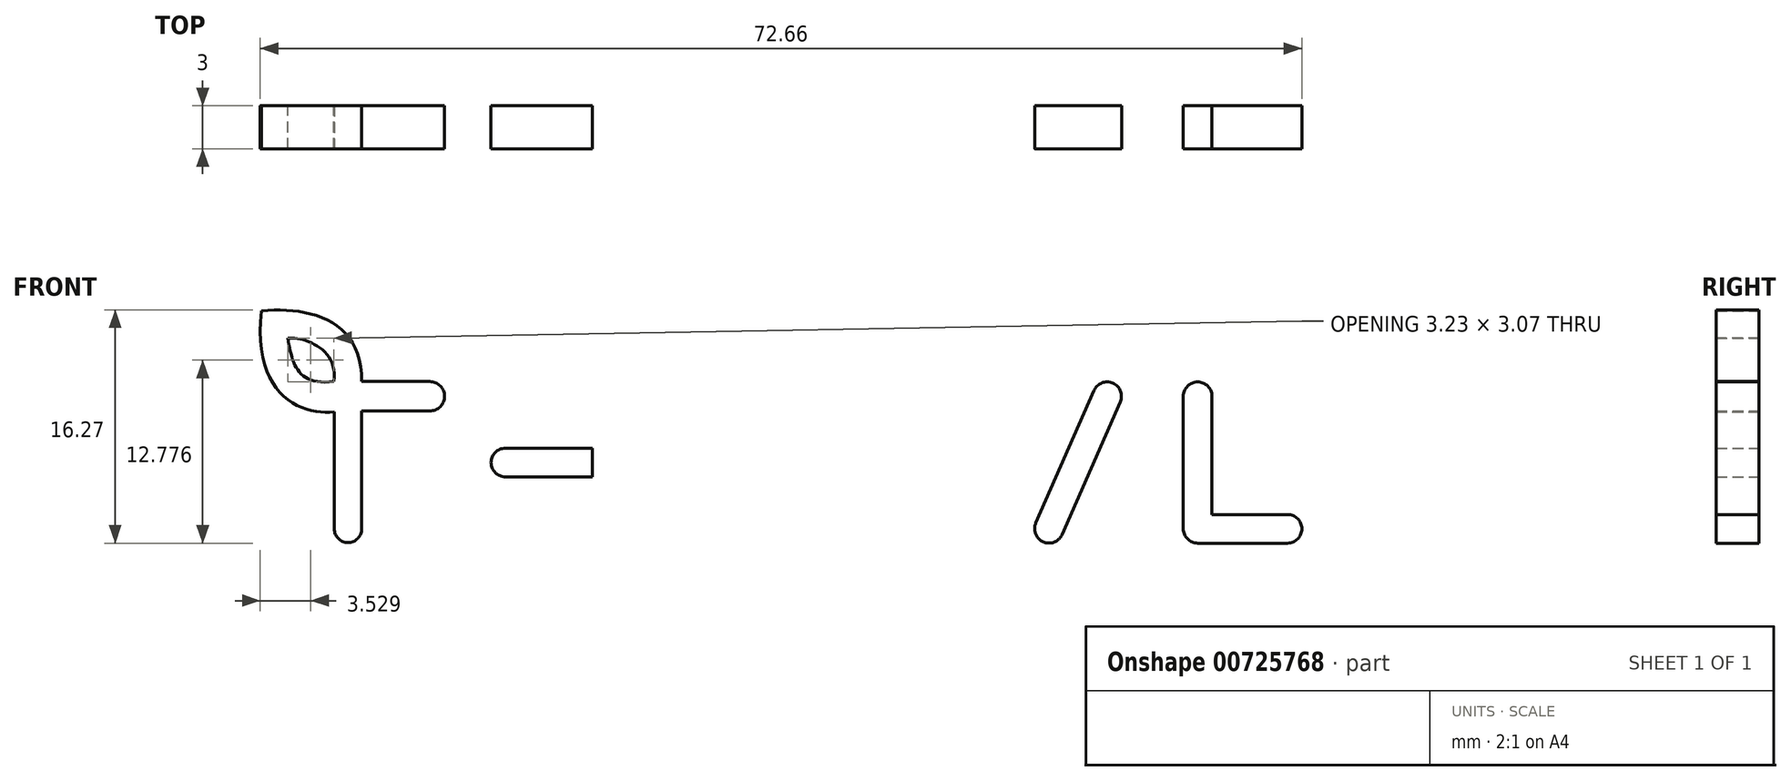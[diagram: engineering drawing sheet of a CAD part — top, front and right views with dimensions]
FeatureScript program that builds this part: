
annotation { "Feature Type Name" : "Feature", "Feature Type Description" : "" }
export const myFeature = defineFeature(function(context is Context, id is Id, definition is map)
    precondition{}
    {
        {
            var Q0;
            Q0=qCreatedBy(makeId("Front.planeOp"),FACE);
            var sketch = newSketch(context, id + "F0", { "sketchPlane" : qUnion([Q0])});
            skLineSegment(sketch, "E0.bottom", {"start": v(0, 0) * mm, "end": v(75, 0) * mm, "construction": true});
            skLineSegment(sketch, "E0.top", {"start": v(0, 50) * mm, "end": v(75, 50) * mm, "construction": true});
            skLineSegment(sketch, "E0.left", {"start": v(0, 0) * mm, "end": v(0, 50) * mm, "construction": true});
            skLineSegment(sketch, "E0.right", {"start": v(75, 0) * mm, "end": v(75, 50) * mm, "construction": true});
            skLineSegment(sketch, "E1", {"start": v(7.84, 1.22) * mm, "end": v(7.84, 9.44) * mm});
            skLineSegment(sketch, "E2", {"start": v(5.93, 1.22) * mm, "end": v(5.93, 9.38) * mm});
            skLineSegment(sketch, "E3", {"start": v(12.6, 9.44) * mm, "end": v(7.84, 9.44) * mm});
            skLineSegment(sketch, "E4", {"start": v(12.6, 11.5) * mm, "end": v(7.84, 11.5) * mm});
            skFitSpline(sketch, "E5", {"points": [v(7.84, 11.5) * mm, v(0.86, 16.42) * mm], "startDerivative": vector(0.22, 12.8) * mm, "endDerivative": vector(-9.91, -1.11) * mm});
            skFitSpline(sketch, "E6", {"points": [v(5.9, 11.5) * mm, v(2.68, 14.53) * mm], "startDerivative": vector(1.06, 6.93) * mm, "endDerivative": vector(-3.29, -0.35) * mm});
            skFitSpline(sketch, "E7", {"points": [v(5.93, 9.38) * mm, v(0.86, 16.42) * mm], "startDerivative": vector(-6.88, -0.84) * mm, "endDerivative": vector(2.12, 17.54) * mm});
            skFitSpline(sketch, "E8", {"points": [v(5.9, 11.5) * mm, v(2.68, 14.53) * mm], "startDerivative": vector(-7.74, -0.96) * mm, "endDerivative": vector(-0.91, 5.16) * mm});
            skArc(sketch, "E9", {"start": v(12.6, 11.5) * mm, "mid": v(13.62, 10.47) * mm, "end": v(12.6, 9.44) * mm});
            skArc(sketch, "E10", {"start": v(5.93, 1.22) * mm, "mid": v(6.89, 0.26) * mm, "end": v(7.84, 1.22) * mm});
            skLineSegment(sketch, "E11", {"start": v(17.86, 10.47) * mm, "end": v(17.86, 1.22) * mm, "construction": true});
            skPoint(sketch, "E11.startSnap0", {"position": v(13.62, 10.47) * mm});
            skLineSegment(sketch, "E12", {"start": v(24.94, 10.47) * mm, "end": v(24.94, 1.22) * mm, "construction": true});
            skLineSegment(sketch, "E13", {"start": v(17.86, 5.85) * mm, "end": v(24.94, 5.85) * mm, "construction": true});
            skArc(sketch, "E14.0.startCap", {"start": v(16.86, 10.47) * mm, "mid": v(17.86, 11.47) * mm, "end": v(18.86, 10.47) * mm});
            skArc(sketch, "E14.0.endCap", {"start": v(18.86, 1.22) * mm, "mid": v(17.86, 0.22) * mm, "end": v(16.86, 1.22) * mm});
            skLineSegment(sketch, "E14.0.left", {"start": v(18.86, 10.47) * mm, "end": v(18.86, 1.22) * mm});
            skLineSegment(sketch, "E14.0.right", {"start": v(16.86, 10.47) * mm, "end": v(16.86, 1.22) * mm});
            skArc(sketch, "E15.0.startCap", {"start": v(17.86, 4.85) * mm, "mid": v(16.86, 5.85) * mm, "end": v(17.86, 6.85) * mm});
            skArc(sketch, "E15.0.endCap", {"start": v(24.94, 6.85) * mm, "mid": v(25.94, 5.85) * mm, "end": v(24.94, 4.85) * mm});
            skLineSegment(sketch, "E15.0.left", {"start": v(17.86, 6.85) * mm, "end": v(24.94, 6.85) * mm});
            skLineSegment(sketch, "E15.0.right", {"start": v(17.86, 4.85) * mm, "end": v(24.94, 4.85) * mm});
            skArc(sketch, "E15.1.startCap", {"start": v(23.94, 10.47) * mm, "mid": v(24.94, 11.47) * mm, "end": v(25.94, 10.47) * mm});
            skArc(sketch, "E15.1.endCap", {"start": v(25.94, 1.22) * mm, "mid": v(24.94, 0.22) * mm, "end": v(23.94, 1.22) * mm});
            skLineSegment(sketch, "E15.1.left", {"start": v(25.94, 10.47) * mm, "end": v(25.94, 1.22) * mm});
            skLineSegment(sketch, "E15.1.right", {"start": v(23.94, 10.47) * mm, "end": v(23.94, 1.22) * mm});
            skLineSegment(sketch, "E16", {"start": v(31.54, 1.22) * mm, "end": v(31.54, 10.47) * mm, "construction": true});
            skLineSegment(sketch, "E17", {"start": v(31.54, 10.47) * mm, "end": v(35.35, 10.47) * mm, "construction": true});
            skLineSegment(sketch, "E18", {"start": v(31.54, 5) * mm, "end": v(35.5, 5) * mm, "construction": true});
            skLineSegment(sketch, "E19", {"start": v(35.5, 5) * mm, "end": v(38.46, 1.22) * mm, "construction": true});
            skFitSpline(sketch, "E20", {"points": [v(35.35, 10.47) * mm, v(35.5, 5) * mm], "startDerivative": vector(12.83, -0.22) * mm, "endDerivative": vector(-12.36, -0.46) * mm, "construction": true});
            skLineSegment(sketch, "E21", {"start": v(45.46, 1.22) * mm, "end": v(45.46, 10.47) * mm, "construction": true});
            skLineSegment(sketch, "E22", {"start": v(51.6, 10.47) * mm, "end": v(55.78, 1.22) * mm, "construction": true});
            skLineSegment(sketch, "E23", {"start": v(55.78, 1.22) * mm, "end": v(59.84, 10.47) * mm, "construction": true});
            skArc(sketch, "E24.0.startCap", {"start": v(50.69, 10.06) * mm, "mid": v(51.18, 11.38) * mm, "end": v(52.5, 10.88) * mm});
            skArc(sketch, "E24.0.endCap", {"start": v(56.7, 1.63) * mm, "mid": v(56.2, 0.31) * mm, "end": v(54.87, 0.8) * mm});
            skLineSegment(sketch, "E24.0.left", {"start": v(52.5, 10.88) * mm, "end": v(56.7, 1.63) * mm});
            skLineSegment(sketch, "E24.0.right", {"start": v(50.69, 10.06) * mm, "end": v(54.87, 0.8) * mm});
            skArc(sketch, "E24.1.startCap", {"start": v(56.7, 0.82) * mm, "mid": v(55.38, 0.3) * mm, "end": v(54.87, 1.62) * mm});
            skArc(sketch, "E24.1.endCap", {"start": v(58.92, 10.87) * mm, "mid": v(60.24, 11.38) * mm, "end": v(60.76, 10.07) * mm});
            skLineSegment(sketch, "E24.1.left", {"start": v(54.87, 1.62) * mm, "end": v(58.92, 10.87) * mm});
            skLineSegment(sketch, "E24.1.right", {"start": v(56.7, 0.82) * mm, "end": v(60.76, 10.07) * mm});
            skArc(sketch, "E25.0.startCap", {"start": v(46.46, 1.22) * mm, "mid": v(45.46, 0.22) * mm, "end": v(44.46, 1.22) * mm});
            skArc(sketch, "E25.0.endCap", {"start": v(44.46, 10.47) * mm, "mid": v(45.46, 11.47) * mm, "end": v(46.46, 10.47) * mm});
            skLineSegment(sketch, "E25.0.left", {"start": v(44.46, 1.22) * mm, "end": v(44.46, 10.47) * mm});
            skLineSegment(sketch, "E25.0.right", {"start": v(46.46, 1.22) * mm, "end": v(46.46, 10.47) * mm});
            skLineSegment(sketch, "E26", {"start": v(66.15, 10.47) * mm, "end": v(72.42, 10.47) * mm, "construction": true});
            skLineSegment(sketch, "E27", {"start": v(66.15, 1.22) * mm, "end": v(72.42, 1.22) * mm, "construction": true});
            skLineSegment(sketch, "E28", {"start": v(66.15, 5.85) * mm, "end": v(71.55, 5.85) * mm, "construction": true});
            skArc(sketch, "E29.0.startCap", {"start": v(66.15, 9.47) * mm, "mid": v(65.15, 10.47) * mm, "end": v(66.15, 11.47) * mm});
            skArc(sketch, "E29.0.endCap", {"start": v(72.42, 11.47) * mm, "mid": v(73.42, 10.47) * mm, "end": v(72.42, 9.47) * mm});
            skLineSegment(sketch, "E29.0.left", {"start": v(66.15, 11.47) * mm, "end": v(72.42, 11.47) * mm});
            skLineSegment(sketch, "E29.0.right", {"start": v(66.15, 9.47) * mm, "end": v(72.42, 9.47) * mm});
            skArc(sketch, "E29.1.startCap", {"start": v(67.15, 1.22) * mm, "mid": v(66.15, 0.22) * mm, "end": v(65.15, 1.22) * mm});
            skArc(sketch, "E29.1.endCap", {"start": v(65.15, 10.47) * mm, "mid": v(66.15, 11.47) * mm, "end": v(67.15, 10.47) * mm});
            skLineSegment(sketch, "E29.1.left", {"start": v(65.15, 1.22) * mm, "end": v(65.15, 10.47) * mm});
            skLineSegment(sketch, "E29.1.right", {"start": v(67.15, 1.22) * mm, "end": v(67.15, 10.47) * mm});
            skArc(sketch, "E29.2.startCap", {"start": v(66.15, 4.85) * mm, "mid": v(65.15, 5.85) * mm, "end": v(66.15, 6.85) * mm});
            skArc(sketch, "E29.2.endCap", {"start": v(71.55, 6.85) * mm, "mid": v(72.55, 5.85) * mm, "end": v(71.55, 4.85) * mm});
            skLineSegment(sketch, "E29.2.left", {"start": v(66.15, 6.85) * mm, "end": v(71.55, 6.85) * mm});
            skLineSegment(sketch, "E29.2.right", {"start": v(66.15, 4.85) * mm, "end": v(71.55, 4.85) * mm});
            skArc(sketch, "E29.3.startCap", {"start": v(66.15, 0.22) * mm, "mid": v(65.15, 1.22) * mm, "end": v(66.15, 2.22) * mm});
            skArc(sketch, "E29.3.endCap", {"start": v(72.42, 2.22) * mm, "mid": v(73.42, 1.22) * mm, "end": v(72.42, 0.22) * mm});
            skLineSegment(sketch, "E29.3.left", {"start": v(66.15, 2.22) * mm, "end": v(72.42, 2.22) * mm});
            skLineSegment(sketch, "E29.3.right", {"start": v(66.15, 0.22) * mm, "end": v(72.42, 0.22) * mm});
            skArc(sketch, "E30.0.startCap", {"start": v(32.54, 1.22) * mm, "mid": v(31.54, 0.22) * mm, "end": v(30.54, 1.22) * mm});
            skArc(sketch, "E30.0.endCap", {"start": v(30.54, 10.47) * mm, "mid": v(30.83, 11.18) * mm, "end": v(31.54, 11.47) * mm});
            skLineSegment(sketch, "E30.0.left", {"start": v(30.54, 1.22) * mm, "end": v(30.54, 10.47) * mm});
            skLineSegment(sketch, "E30.0.right", {"start": v(32.54, 1.22) * mm, "end": v(32.54, 4) * mm});
            skArc(sketch, "E30.1.endCap", {"start": v(39.24, 1.83) * mm, "mid": v(39.07, 0.44) * mm, "end": v(37.68, 0.61) * mm});
            skLineSegment(sketch, "E30.1.left", {"start": v(37.26, 4.36) * mm, "end": v(39.24, 1.83) * mm});
            skLineSegment(sketch, "E30.1.right", {"start": v(35.03, 4) * mm, "end": v(37.68, 0.61) * mm});
            skLineSegment(sketch, "E31.0.left", {"start": v(31.54, 11.47) * mm, "end": v(35.37, 11.47) * mm});
            skLineSegment(sketch, "E31.0.right", {"start": v(32.54, 9.47) * mm, "end": v(35.35, 9.47) * mm});
            skFitSpline(sketch, "E31.1.left", {"points": [v(35.37, 11.47) * mm, v(36, 11.46) * mm, v(37.17, 11.24) * mm, v(38.53, 10.4) * mm, v(39.37, 9.18) * mm, v(39.67, 7.78) * mm, v(39.41, 6.38) * mm, v(38.61, 5.14) * mm, v(37.3, 4.27) * mm, v(36.16, 4.03) * mm, v(35.54, 4) * mm]});
            skFitSpline(sketch, "E31.1.right", {"points": [v(35.33, 9.47) * mm, v(35.77, 9.46) * mm, v(36.47, 9.32) * mm, v(37.12, 8.9) * mm, v(37.49, 8.36) * mm, v(37.62, 7.75) * mm, v(37.5, 7.14) * mm, v(37.16, 6.6) * mm, v(36.54, 6.17) * mm, v(35.88, 6.02) * mm, v(35.47, 6) * mm]});
            skLineSegment(sketch, "E31.2.right", {"start": v(32.54, 4) * mm, "end": v(35.03, 4) * mm});
            skLineSegment(sketch, "E32.trimOffspring", {"start": v(32.54, 6) * mm, "end": v(35.47, 6) * mm});
            skLineSegment(sketch, "E33.trimOffspring", {"start": v(32.54, 6) * mm, "end": v(32.54, 9.47) * mm});
            skSolve(sketch);
        }
        {
            var Q0;
            Q0=makeQuery(id+"F0.imprint","IMPRINT",FACE,{"disambiguationData":[TD([[makeQuery(id+"F0.imprint","IMPRINT",EDGE,{"derivedFrom":sQuery(id+"F0.wireOp",EDGE,"E1")}),1.0]])]});
            var Q1;
            {var subQ0=sQuery(id+"F0.wireOp",EDGE,"E15.0.left");var subQ3=sQuery(id+"F0.wireOp",EDGE,"E14.0.left");var subQ4=makeQuery(id+"F0.imprint","INTERSECT",VERTEX,{"derivedFrom":[subQ3,subQ0]});Q1=makeQuery(id+"F0.imprint","IMPRINT",FACE,{"disambiguationData":[TD([[makeQuery(id+"F0.imprint","IMPRINT",EDGE,{"disambiguationData":[TD([[subQ4,-1.0]])],"derivedFrom":subQ3}),-1.0]])]});}
            var Q2;
            {var subQ0=sQuery(id+"F0.wireOp",EDGE,"E15.1.endCap");Q2=makeQuery(id+"F0.imprint","IMPRINT",FACE,{"disambiguationData":[TD([[makeQuery(id+"F0.imprint","IMPRINT",EDGE,{"derivedFrom":subQ0}),-1.0]])]});}
            var Q3;
            {var subQ0=sQuery(id+"F0.wireOp",EDGE,"E15.0.left");var subQ1=sQuery(id+"F0.wireOp",EDGE,"E14.0.left");var subQ2=makeQuery(id+"F0.imprint","INTERSECT",VERTEX,{"derivedFrom":[subQ1,subQ0]});Q3=makeQuery(id+"F0.imprint","IMPRINT",FACE,{"disambiguationData":[TD([[makeQuery(id+"F0.imprint","IMPRINT",EDGE,{"disambiguationData":[TD([[subQ2,-1.0]])],"derivedFrom":subQ1}),1.0]])]});}
            var Q4;
            {var subQ6=sQuery(id+"F0.wireOp",EDGE,"E14.0.startCap");Q4=makeQuery(id+"F0.imprint","IMPRINT",FACE,{"disambiguationData":[TD([[makeQuery(id+"F0.imprint","IMPRINT",EDGE,{"derivedFrom":subQ6}),-1.0]])]});}
            var Q5;
            {var subQ6=sQuery(id+"F0.wireOp",EDGE,"E14.0.endCap");Q5=makeQuery(id+"F0.imprint","IMPRINT",FACE,{"disambiguationData":[TD([[makeQuery(id+"F0.imprint","IMPRINT",EDGE,{"derivedFrom":subQ6}),-1.0]])]});}
            var Q6;
            {var subQ0=sQuery(id+"F0.wireOp",EDGE,"E15.1.startCap");Q6=makeQuery(id+"F0.imprint","IMPRINT",FACE,{"disambiguationData":[TD([[makeQuery(id+"F0.imprint","IMPRINT",EDGE,{"derivedFrom":subQ0}),-1.0]])]});}
            var Q7;
            {var subQ1=sQuery(id+"F0.wireOp",EDGE,"E15.0.endCap");var subQ5=sQuery(id+"F0.wireOp",EDGE,"E15.0.left");var subQ6=makeQuery(id+"F0.imprint","INTERSECT",VERTEX,{"derivedFrom":[subQ1,subQ5]});Q7=makeQuery(id+"F0.imprint","IMPRINT",FACE,{"disambiguationData":[TD([[makeQuery(id+"F0.imprint","IMPRINT",EDGE,{"disambiguationData":[TD([[subQ6,-1.0]])],"derivedFrom":subQ1}),-1.0]])]});}
            var Q8;
            Q8=makeQuery(id+"F0.imprint","IMPRINT",FACE,{"disambiguationData":[TD([[makeQuery(id+"F0.imprint","IMPRINT",EDGE,{"derivedFrom":sQuery(id+"F0.wireOp",EDGE,"E25.0.startCap")}),-1.0]])]});
            var Q9;
            {var subQ5=sQuery(id+"F0.wireOp",EDGE,"E24.0.startCap");Q9=makeQuery(id+"F0.imprint","IMPRINT",FACE,{"disambiguationData":[TD([[makeQuery(id+"F0.imprint","IMPRINT",EDGE,{"derivedFrom":subQ5}),-1.0]])]});}
            var Q10;
            {var subQ4=sQuery(id+"F0.wireOp",EDGE,"E24.0.endCap");Q10=makeQuery(id+"F0.imprint","IMPRINT",FACE,{"disambiguationData":[TD([[makeQuery(id+"F0.imprint","IMPRINT",EDGE,{"derivedFrom":subQ4}),1.0]])]});}
            var Q11;
            {var subQ1=sQuery(id+"F0.wireOp",EDGE,"E24.0.endCap");Q11=makeQuery(id+"F0.imprint","IMPRINT",FACE,{"disambiguationData":[TD([[makeQuery(id+"F0.imprint","IMPRINT",EDGE,{"derivedFrom":subQ1}),-1.0]])]});}
            var Q12;
            {var subQ1=sQuery(id+"F0.wireOp",EDGE,"E29.0.startCap");Q12=makeQuery(id+"F0.imprint","IMPRINT",FACE,{"disambiguationData":[TD([[makeQuery(id+"F0.imprint","IMPRINT",EDGE,{"derivedFrom":subQ1}),1.0]])]});}
            var Q13;
            {var subQ1=sQuery(id+"F0.wireOp",EDGE,"E29.0.endCap");Q13=makeQuery(id+"F0.imprint","IMPRINT",FACE,{"disambiguationData":[TD([[makeQuery(id+"F0.imprint","IMPRINT",EDGE,{"derivedFrom":subQ1}),-1.0]])]});}
            var Q14;
            {var subQ5=sQuery(id+"F0.wireOp",EDGE,"E29.2.endCap");Q14=makeQuery(id+"F0.imprint","IMPRINT",FACE,{"disambiguationData":[TD([[makeQuery(id+"F0.imprint","IMPRINT",EDGE,{"derivedFrom":subQ5}),-1.0]])]});}
            var Q15;
            {var subQ4=sQuery(id+"F0.wireOp",EDGE,"E29.1.startCap");Q15=makeQuery(id+"F0.imprint","IMPRINT",FACE,{"disambiguationData":[TD([[makeQuery(id+"F0.imprint","IMPRINT",EDGE,{"derivedFrom":subQ4}),1.0]])]});}
            var Q16;
            {var subQ3=sQuery(id+"F0.wireOp",EDGE,"E29.1.right");var subQ6=sQuery(id+"F0.wireOp",EDGE,"E29.2.right");var subQ8=makeQuery(id+"F0.imprint","INTERSECT",VERTEX,{"derivedFrom":[subQ3,subQ6]});Q16=makeQuery(id+"F0.imprint","IMPRINT",FACE,{"disambiguationData":[TD([[makeQuery(id+"F0.imprint","IMPRINT",EDGE,{"disambiguationData":[TD([[subQ8,-1.0]])],"derivedFrom":subQ3}),1.0]])]});}
            var Q17;
            {var subQ5=sQuery(id+"F0.wireOp",EDGE,"E29.1.left");var subQ9=sQuery(id+"F0.wireOp",EDGE,"E29.3.startCap");var subQ10=makeQuery(id+"F0.imprint","INTERSECT",VERTEX,{"derivedFrom":[subQ5,subQ9]});Q17=makeQuery(id+"F0.imprint","IMPRINT",FACE,{"disambiguationData":[TD([[makeQuery(id+"F0.imprint","IMPRINT",EDGE,{"disambiguationData":[TD([[subQ10,-1.0]])],"derivedFrom":subQ5}),-1.0]])]});}
            var Q18;
            {var subQ4=sQuery(id+"F0.wireOp",EDGE,"E29.1.startCap");Q18=makeQuery(id+"F0.imprint","IMPRINT",FACE,{"disambiguationData":[TD([[makeQuery(id+"F0.imprint","IMPRINT",EDGE,{"derivedFrom":subQ4}),-1.0]])]});}
            var Q19;
            {var subQ4=sQuery(id+"F0.wireOp",EDGE,"E29.0.startCap");Q19=makeQuery(id+"F0.imprint","IMPRINT",FACE,{"disambiguationData":[TD([[makeQuery(id+"F0.imprint","IMPRINT",EDGE,{"derivedFrom":subQ4}),-1.0]])]});}
            var Q20;
            Q20=makeQuery(id+"F0.imprint","IMPRINT",FACE,{"disambiguationData":[TD([[makeQuery(id+"F0.imprint","IMPRINT",EDGE,{"derivedFrom":sQuery(id+"F0.wireOp",EDGE,"E30.0.startCap")}),-1.0]])]});
            extrude(context, id + "F1", {"entities" : qUnion([Q0, Q1, Q2, Q3, Q4, Q5, Q6, Q7, Q8, Q9, Q10, Q11, Q12, Q13, Q14, Q15, Q16, Q17, Q18, Q19, Q20]), "depth" : 3 * mm, "offsetDistance" : 25 * mm});
        }
    });
